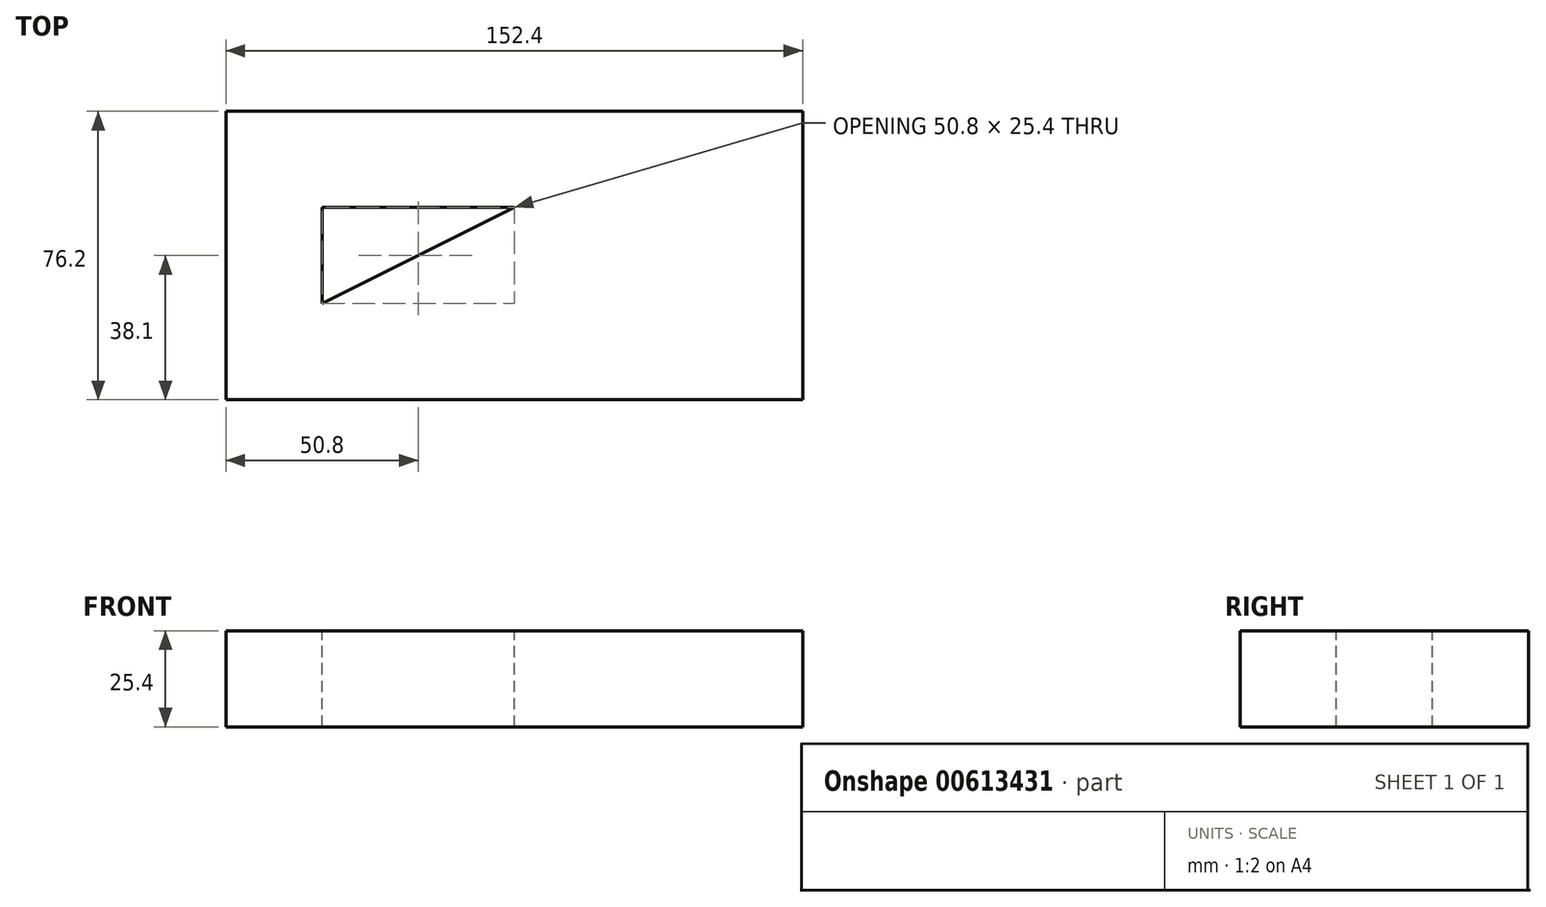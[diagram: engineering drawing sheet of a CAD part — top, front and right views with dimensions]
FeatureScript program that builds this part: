
annotation { "Feature Type Name" : "Feature", "Feature Type Description" : "" }
export const myFeature = defineFeature(function(context is Context, id is Id, definition is map)
    precondition{}
    {
        {
            var Q0;
            Q0=qCreatedBy(makeId("Front.planeOp"),FACE);
            var sketch = newSketch(context, id + "F0", { "sketchPlane" : qUnion([Q0])});
            skLineSegment(sketch, "E0", {"start": v(0, 0) * mm, "end": v(0, 50.8) * mm});
            skLineSegment(sketch, "E1", {"start": v(0, 50.8) * mm, "end": v(25.4, 50.8) * mm});
            skLineSegment(sketch, "E2", {"start": v(25.4, 50.8) * mm, "end": v(152.4, 50.8) * mm});
            skLineSegment(sketch, "E3", {"start": v(152.4, 50.8) * mm, "end": v(152.4, 0) * mm});
            skLineSegment(sketch, "E4", {"start": v(152.4, 0) * mm, "end": v(0, 0) * mm});
            skLineSegment(sketch, "E5", {"start": v(25.4, 0) * mm, "end": v(25.4, 25.4) * mm});
            skLineSegment(sketch, "E6", {"start": v(25.4, 25.4) * mm, "end": v(76.2, 25.4) * mm});
            skLineSegment(sketch, "E7", {"start": v(76.2, 25.4) * mm, "end": v(76.2, 0) * mm});
            skLineSegment(sketch, "E8", {"start": v(25.4, 50.8) * mm, "end": v(25.4, 25.4) * mm});
            skSolve(sketch);
        }
        {
            var Q0;
            {var subQ2=sQuery(id+"F0.wireOp",EDGE,"E0");Q0=makeQuery(id+"F0.imprint","IMPRINT",FACE,{"disambiguationData":[TD([[makeQuery(id+"F0.imprint","IMPRINT",EDGE,{"derivedFrom":subQ2}),-1.0]])]});}
            var Q1;
            Q1=makeQuery(id+"F0.imprint","IMPRINT",FACE,{"disambiguationData":[TD([[makeQuery(id+"F0.imprint","IMPRINT",EDGE,{"derivedFrom":sQuery(id+"F0.wireOp",EDGE,"E2")}),-1.0]])]});
            var Q2;
            {var subQ0=sQuery(id+"F0.wireOp",EDGE,"E5");Q2=makeQuery(id+"F0.imprint","IMPRINT",FACE,{"disambiguationData":[TD([[makeQuery(id+"F0.imprint","IMPRINT",EDGE,{"derivedFrom":subQ0}),-1.0]])]});}
            extrude(context, id + "F1", {"entities" : qUnion([Q0, Q1, Q2]), "oppositeDirection" : true, "depth" : 76.2 * mm, "offsetDistance" : 25.4 * mm});
        }
        {
            var Q0;
            Q0=makeQuery(id+"F1.opExtrude","SWEPT_FACE",FACE,{"disambiguationData":[OSD([sQuery(id+"F0.wireOp",EDGE,"E1"),sQuery(id+"F0.wireOp",EDGE,"E2")])]});
            var sketch = newSketch(context, id + "F2", { "sketchPlane" : qUnion([Q0])});
            skLineSegment(sketch, "E9", {"start": v(152.4, 76.2) * mm, "end": v(152.4, 50.8) * mm});
            skLineSegment(sketch, "E10", {"start": v(152.4, 50.8) * mm, "end": v(25.4, 50.8) * mm});
            skLineSegment(sketch, "E11", {"start": v(25.4, 50.8) * mm, "end": v(25.4, 0) * mm});
            skLineSegment(sketch, "E12", {"start": v(25.4, 0) * mm, "end": v(25.4, 25.4) * mm});
            skLineSegment(sketch, "E13", {"start": v(25.4, 50.8) * mm, "end": v(76.2, 50.8) * mm});
            skLineSegment(sketch, "E14", {"start": v(76.2, 50.8) * mm, "end": v(25.4, 25.4) * mm});
            skSolve(sketch);
        }
        {
            var Q0;
            {var subQ4=sQuery(id+"F2.wireOp",EDGE,"E10");Q0=makeQuery(id+"F2.imprint","IMPRINT",FACE,{"disambiguationData":[TD([[makeQuery(id+"F2.imprint","IMPRINT",EDGE,{"derivedFrom":subQ4}),1.0]])]});}
            extrude(context, id + "F3", {"entities" : qUnion([Q0]), "operationType" : NewBodyOperationType.REMOVE, "oppositeDirection" : true, "depth" : 76.2 * mm, "offsetDistance" : 25.4 * mm});
        }
        {
            var Q0;
            Q0=makeQuery(id+"F1.opExtrude","SWEPT_FACE",FACE,{"disambiguationData":[OSD([sQuery(id+"F0.wireOp",EDGE,"E1"),sQuery(id+"F0.wireOp",EDGE,"E2")])]});
            var sketch = newSketch(context, id + "F4", { "sketchPlane" : qUnion([Q0])});
            skLineSegment(sketch, "E15", {"start": v(25.4, 25.4) * mm, "end": v(25.4, 50.8) * mm});
            skLineSegment(sketch, "E16", {"start": v(25.4, 50.8) * mm, "end": v(76.2, 50.8) * mm});
            skSolve(sketch);
        }
        {
            var Q0;
            Q0=makeQuery(id+"F4.imprint","IMPRINT",FACE,{"disambiguationData":[TD([[makeQuery(id+"F4.imprint","IMPRINT",EDGE,{"derivedFrom":sQuery(id+"F4.wireOp",EDGE,"E15")}),-1.0]])]});
            extrude(context, id + "F5", {"entities" : qUnion([Q0]), "operationType" : NewBodyOperationType.REMOVE, "oppositeDirection" : true, "depth" : 25.4 * mm, "offsetDistance" : 25.4 * mm});
        }
    });
